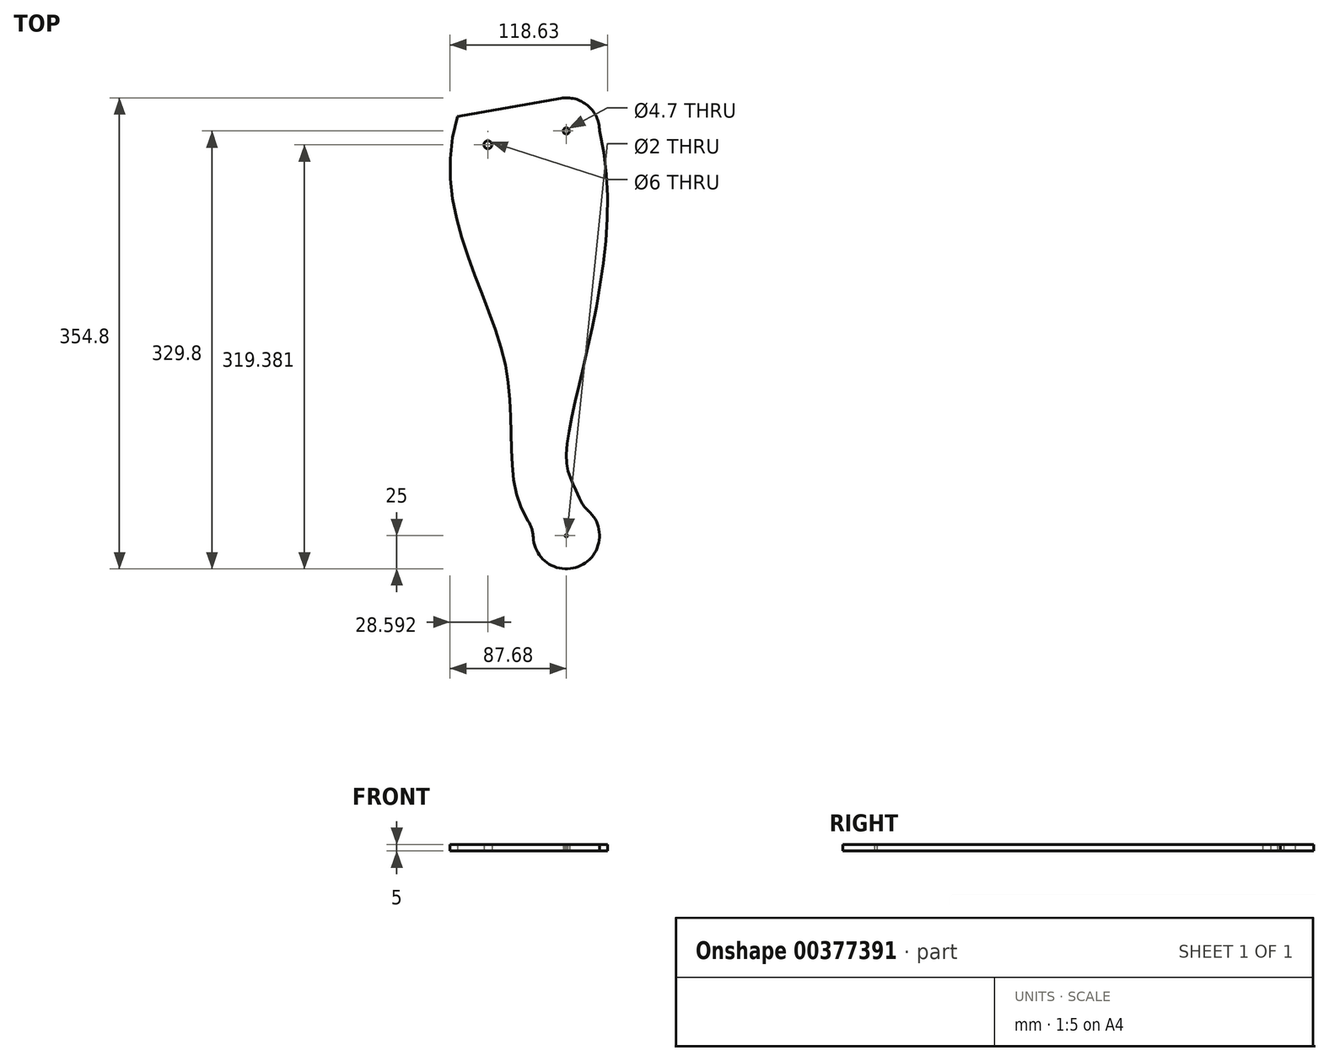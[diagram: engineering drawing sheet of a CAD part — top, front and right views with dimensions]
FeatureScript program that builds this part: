
annotation { "Feature Type Name" : "Feature", "Feature Type Description" : "" }
export const myFeature = defineFeature(function(context is Context, id is Id, definition is map)
    precondition{}
    {
        {
            var Q0;
            Q0=qCreatedBy(makeId("Top.planeOp"),FACE);
            var sketch = newSketch(context, id + "F0", { "sketchPlane" : qUnion([Q0])});
            skCircle(sketch, "E0", {"center": v(0, 0) * mm, "radius": 2.35 * mm});
            skArc(sketch, "E1", {"start": v(-24.44, -299.53) * mm, "mid": v(10.45, -327.51) * mm, "end": v(11.9, -282.81) * mm});
            skArc(sketch, "E2", {"start": v(25, 0) * mm, "mid": v(16.07, 19.15) * mm, "end": v(-4.34, 24.62) * mm});
            skLineSegment(sketch, "E3", {"start": v(-4.34, 24.62) * mm, "end": v(-82.12, 10.9) * mm});
            skLineSegment(sketch, "E4", {"start": v(-87.68, 20.59) * mm, "end": v(-87.68, -140.16) * mm, "construction": true});
            skLineSegment(sketch, "E5", {"start": v(-24.44, -299.53) * mm, "end": v(11.9, -282.81) * mm, "construction": true});
            skCircle(sketch, "E6", {"center": v(0, -304.8) * mm, "radius": 1 * mm});
            skFitSpline(sketch, "E7", {"points": [v(25, 0) * mm, v(0, -244.2) * mm, v(11.9, -282.81) * mm], "startDerivative": vector(93.1, -381.9) * mm, "endDerivative": vector(50.34, -171.54) * mm});
            skFitSpline(sketch, "E8", {"points": [v(-82.12, 10.9) * mm, v(-45.47, -178.53) * mm, v(-24.44, -299.53) * mm], "startDerivative": vector(-115.76, -382.46) * mm, "endDerivative": vector(173.9, -207.44) * mm});
            skLineSegment(sketch, "E9", {"start": v(30.95, -10.57) * mm, "end": v(30.95, -105.63) * mm, "construction": true});
            skSolve(sketch);
        }
        {
            var Q0;
            Q0=qCreatedBy(makeId("Top.planeOp"),FACE);
            var sketch = newSketch(context, id + "F1", { "sketchPlane" : qUnion([Q0])});
            skLineSegment(sketch, "E10", {"start": v(0, 0) * mm, "end": v(-59.09, -10.42) * mm, "construction": true});
            skCircle(sketch, "E11", {"center": v(-59.09, -10.42) * mm, "radius": 3 * mm});
            skSolve(sketch);
        }
        {
            var Q0;
            Q0 = qSketchRegion(id + "F0", true);
            extrude(context, id + "F2", {"entities" : qUnion([Q0]), "depth" : 5 * mm});
        }
        {
            var Q0;
            Q0 = qSketchRegion(id + "F1", true);
            extrude(context, id + "F3", {"entities" : qUnion([Q0]), "operationType" : NewBodyOperationType.REMOVE, "endBound" : BoundingType.THROUGH_ALL, "depth" : 25 * mm});
        }
        {
            var Q0;
            Q0=makeQuery(id+"F2.opExtrude","SWEPT_EDGE",EDGE,{"disambiguationData":[OSD([sQuery(id+"F0.wireOp",EDGE,"E1"),sQuery(id+"F0.wireOp",EDGE,"IRwkBBPc-iLYB-gRdi-gAcp-Ph2cs2GShcop")])]});
            var Q1;
            Q1=makeQuery(id+"F2.opExtrude","SWEPT_EDGE",EDGE,{"disambiguationData":[OSD([sQuery(id+"F0.wireOp",EDGE,"E1"),sQuery(id+"F0.wireOp",EDGE,"1044895b-140e-4190-b1e2-f8b0b1552d9c")])]});
            fillet(context, id + "F4", {"entities" : qUnion([Q0, Q1]), "radius" : 25 * mm, "tangentPropagation" : true, "allowEdgeOverflow" : false});
        }
    });
